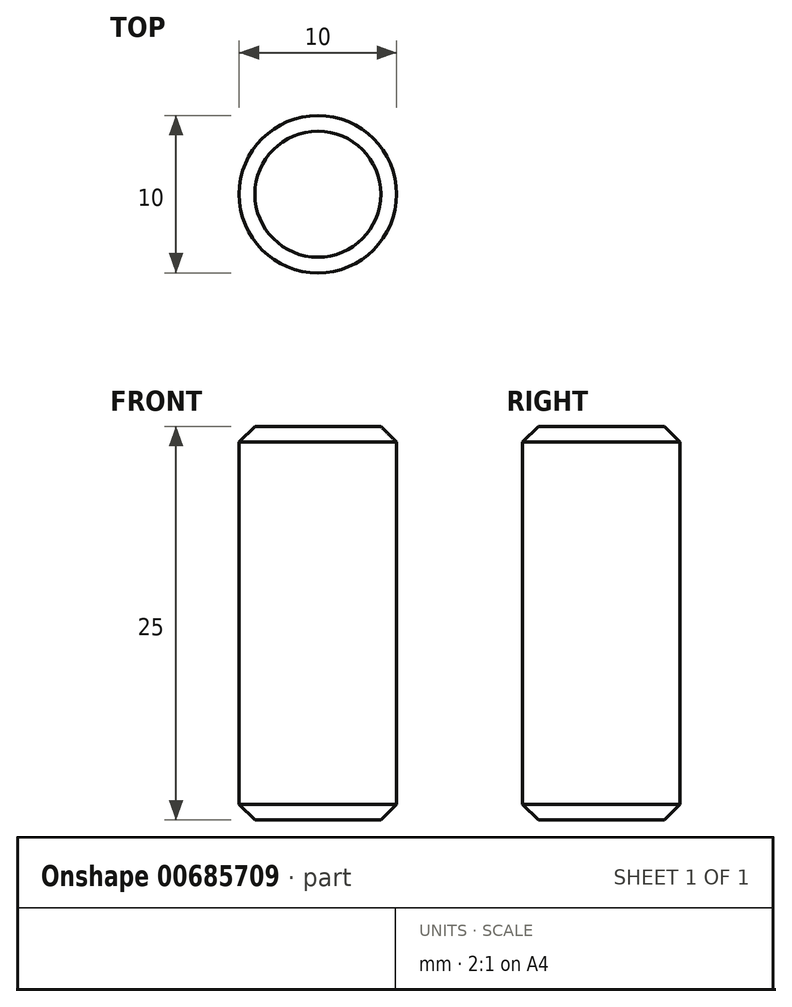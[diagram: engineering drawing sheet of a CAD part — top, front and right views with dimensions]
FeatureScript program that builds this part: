
annotation { "Feature Type Name" : "Feature", "Feature Type Description" : "" }
export const myFeature = defineFeature(function(context is Context, id is Id, definition is map)
    precondition{}
    {
        {
            var Q0;
            Q0=qCreatedBy(makeId("Top.planeOp"),FACE);
            var sketch = newSketch(context, id + "F0", { "sketchPlane" : qUnion([Q0])});
            skCircle(sketch, "E0", {"center": v(0, 0) * mm, "radius": 5 * mm});
            skSolve(sketch);
        }
        {
            var Q0;
            Q0=makeQuery(id+"F0.imprint","IMPRINT",FACE,{"disambiguationData":[TD([[makeQuery(id+"F0.imprint","IMPRINT",EDGE,{"derivedFrom":sQuery(id+"F0.wireOp",EDGE,"E0")}),1.0]])]});
            extrude(context, id + "F1", {"entities" : qUnion([Q0]), "depth" : 25 * mm, "offsetDistance" : 25 * mm});
        }
        {
            var Q0;
            Q0=makeQuery(id+"F1.opExtrude","SWEPT_FACE",FACE,{"disambiguationData":[OSD([sQuery(id+"F0.wireOp",EDGE,"E0")])]});
            chamfer(context, id + "F2", {"entities" : qUnion([Q0]), "width" : 1 * mm, "tangentPropagation" : true});
        }
    });
